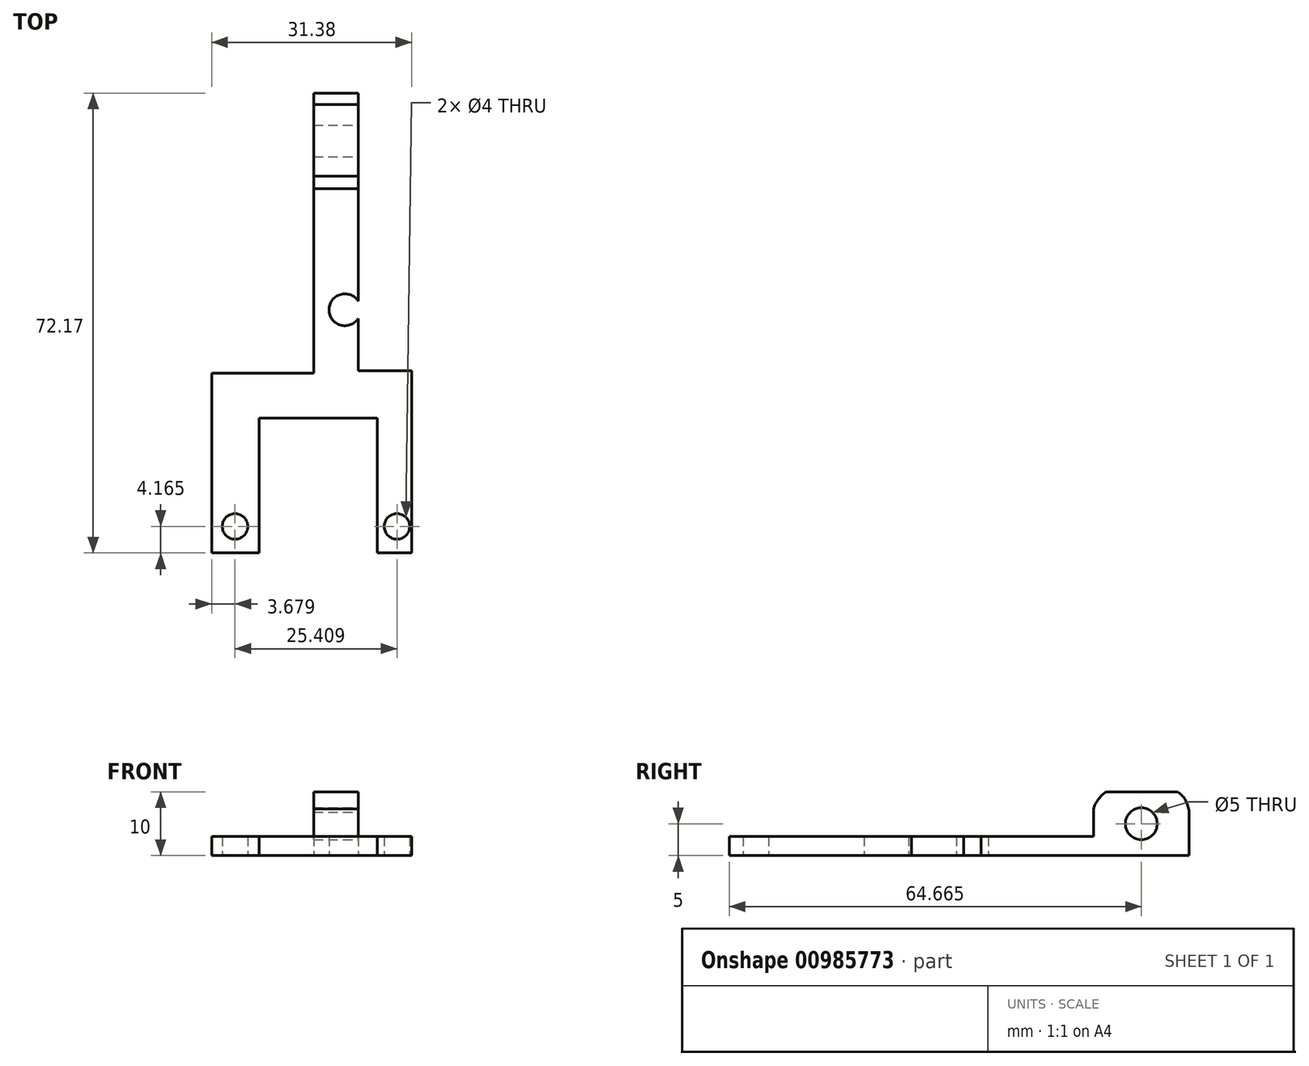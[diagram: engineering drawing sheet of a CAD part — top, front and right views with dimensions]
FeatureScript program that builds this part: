
annotation { "Feature Type Name" : "Feature", "Feature Type Description" : "" }
export const myFeature = defineFeature(function(context is Context, id is Id, definition is map)
    precondition{}
    {
        {
            assignVariable(context, id + "F0", {"name" : "thickness", "anyValue" : 3});
        }
        {
            var Q0;
            Q0=qCreatedBy(makeId("Top.planeOp"),FACE);
            var sketch = newSketch(context, id + "F1", { "sketchPlane" : qUnion([Q0])});
            skLineSegment(sketch, "E0", {"start": v(-1.74, 48.16) * mm, "end": v(-1.74, 4.18) * mm});
            skLineSegment(sketch, "E1", {"start": v(-1.74, 4.18) * mm, "end": v(-17.74, 4.18) * mm});
            skLineSegment(sketch, "E2", {"start": v(-17.74, 4.18) * mm, "end": v(-17.74, -24.01) * mm});
            skLineSegment(sketch, "E3", {"start": v(-17.74, -24.01) * mm, "end": v(-10.3, -24.01) * mm});
            skLineSegment(sketch, "E4", {"start": v(-10.3, -24.01) * mm, "end": v(-10.3, -2.82) * mm});
            skLineSegment(sketch, "E5", {"start": v(-10.3, -2.82) * mm, "end": v(8.29, -2.82) * mm});
            skLineSegment(sketch, "E6", {"start": v(8.29, -2.82) * mm, "end": v(8.29, -24.01) * mm});
            skLineSegment(sketch, "E7", {"start": v(8.29, -24.01) * mm, "end": v(13.64, -24.01) * mm});
            skLineSegment(sketch, "E8", {"start": v(13.64, -24.01) * mm, "end": v(13.64, 4.56) * mm});
            skLineSegment(sketch, "E9", {"start": v(13.64, 4.56) * mm, "end": v(5.26, 4.56) * mm});
            skLineSegment(sketch, "E10", {"start": v(5.26, 48.16) * mm, "end": v(-1.74, 48.16) * mm});
            skCircle(sketch, "E11", {"center": v(-14.06, -19.84) * mm, "radius": 2 * mm});
            skCircle(sketch, "E12", {"center": v(11.35, -19.84) * mm, "radius": 2 * mm});
            skLineSegment(sketch, "E13.trimOffspring", {"start": v(5.26, 15.53) * mm, "end": v(5.26, 48.16) * mm});
            skLineSegment(sketch, "E14", {"start": v(5.26, 4.56) * mm, "end": v(5.26, 12.78) * mm});
            skArc(sketch, "E15", {"start": v(5.26, 15.53) * mm, "mid": v(0.67, 14.16) * mm, "end": v(5.26, 12.78) * mm});
            skSolve(sketch);
        }
        {
            var Q0;
            Q0=makeQuery(id+"F1.imprint","IMPRINT",FACE,{"disambiguationData":[TD([[makeQuery(id+"F1.imprint","IMPRINT",EDGE,{"derivedFrom":sQuery(id+"F1.wireOp",EDGE,"E0")}),1.0]])]});
            extrude(context, id + "F2", {"entities" : qUnion([Q0]), "depth" : (getVariable(context, 'thickness')) * mm, "offsetDistance" : 25 * mm});
        }
        {
            var Q0;
            Q0=makeQuery(id+"F2.opExtrude","CAP_FACE",FACE,{"disambiguationData":[OSD([sQuery(id+"F1.wireOp",EDGE,"E0"),sQuery(id+"F1.wireOp",EDGE,"E1"),sQuery(id+"F1.wireOp",EDGE,"E2"),sQuery(id+"F1.wireOp",EDGE,"E3"),sQuery(id+"F1.wireOp",EDGE,"E4"),sQuery(id+"F1.wireOp",EDGE,"E5"),sQuery(id+"F1.wireOp",EDGE,"E6"),sQuery(id+"F1.wireOp",EDGE,"E7"),sQuery(id+"F1.wireOp",EDGE,"E8"),sQuery(id+"F1.wireOp",EDGE,"E9"),sQuery(id+"F1.wireOp",EDGE,"E10"),sQuery(id+"F1.wireOp",EDGE,"E11"),sQuery(id+"F1.wireOp",EDGE,"E12"),sQuery(id+"F1.wireOp",EDGE,"E13.trimOffspring"),sQuery(id+"F1.wireOp",EDGE,"E14"),sQuery(id+"F1.wireOp",EDGE,"E15")])],"isStart":false});
            var sketch = newSketch(context, id + "F3", { "sketchPlane" : qUnion([Q0])});
            skLineSegment(sketch, "E16.bottom", {"start": v(-1.74, 48.16) * mm, "end": v(5.26, 48.16) * mm});
            skLineSegment(sketch, "E16.top", {"start": v(-1.74, 33.16) * mm, "end": v(5.26, 33.16) * mm});
            skLineSegment(sketch, "E16.left", {"start": v(-1.74, 48.16) * mm, "end": v(-1.74, 33.16) * mm});
            skLineSegment(sketch, "E16.right", {"start": v(5.26, 48.16) * mm, "end": v(5.26, 33.16) * mm});
            skSolve(sketch);
        }
        {
            var Q0;
            Q0=makeQuery(id+"F3.imprint","IMPRINT",FACE,{"disambiguationData":[TD([[makeQuery(id+"F3.imprint","IMPRINT",EDGE,{"derivedFrom":sQuery(id+"F3.wireOp",EDGE,"E16.bottom")}),1.0]])]});
            extrude(context, id + "F4", {"entities" : qUnion([Q0]), "operationType" : NewBodyOperationType.ADD, "depth" : (10 - getVariable(context, 'thickness')) * mm, "offsetDistance" : 25 * mm});
        }
        {
            var Q0;
            Q0=makeQuery(id+"F4.boolean.opBoolean","MERGE",FACE,{"derivedFrom":[makeQuery(id+"F2.opExtrude","SWEPT_FACE",FACE,{"disambiguationData":[OSD([sQuery(id+"F1.wireOp",EDGE,"E13.trimOffspring")])]}),makeQuery(id+"F4.opExtrude","SWEPT_FACE",FACE,{"disambiguationData":[OSD([sQuery(id+"F3.wireOp",EDGE,"E16.right")])]})]});
            var sketch = newSketch(context, id + "F5", { "sketchPlane" : qUnion([Q0])});
            skCircle(sketch, "E17", {"center": v(40.66, 5) * mm, "radius": 2.5 * mm});
            skPoint(sketch, "E18", {"position": v(40.66, 10) * mm});
            skPoint(sketch, "E19", {"position": v(48.16, 5) * mm});
            skSolve(sketch);
        }
        {
            var Q0;
            Q0=makeQuery(id+"F5.imprint","IMPRINT",FACE,{"disambiguationData":[TD([[makeQuery(id+"F5.imprint","IMPRINT",EDGE,{"derivedFrom":sQuery(id+"F5.wireOp",EDGE,"E17")}),1.0]])]});
            var Q1;
            Q1=makeQuery(id+"F4.boolean.opBoolean","MERGE",FACE,{"derivedFrom":[makeQuery(id+"F2.opExtrude","SWEPT_FACE",FACE,{"disambiguationData":[OSD([sQuery(id+"F1.wireOp",EDGE,"E0")])]}),makeQuery(id+"F4.opExtrude","SWEPT_FACE",FACE,{"disambiguationData":[OSD([sQuery(id+"F3.wireOp",EDGE,"E16.left")])]})]});
            extrude(context, id + "F6", {"entities" : qUnion([Q0]), "operationType" : NewBodyOperationType.REMOVE, "endBound" : BoundingType.UP_TO_SURFACE, "oppositeDirection" : true, "depth" : 25 * mm, "endBoundEntityFace" : qUnion([Q1]), "offsetDistance" : 25 * mm});
        }
        {
            var Q0;
            Q0=makeQuery(id+"F4.boolean.opBoolean","MERGE",FACE,{"derivedFrom":[makeQuery(id+"F2.opExtrude","SWEPT_FACE",FACE,{"disambiguationData":[OSD([sQuery(id+"F1.wireOp",EDGE,"E13.trimOffspring")])]}),makeQuery(id+"F4.opExtrude","SWEPT_FACE",FACE,{"disambiguationData":[OSD([sQuery(id+"F3.wireOp",EDGE,"E16.right")])]})]});
            var sketch = newSketch(context, id + "F7", { "sketchPlane" : qUnion([Q0])});
            skArc(sketch, "E20", {"start": v(35.1, 10) * mm, "mid": v(33.92, 8.83) * mm, "end": v(33.16, 7.35) * mm});
            skArc(sketch, "E21", {"start": v(48.16, 6.84) * mm, "mid": v(47.63, 8.62) * mm, "end": v(46.38, 10) * mm});
            skSolve(sketch);
        }
        {
            var Q0;
            {var subQ0=sQuery(id+"F7.wireOp",EDGE,"E20");Q0=makeQuery(id+"F7.imprint","IMPRINT",FACE,{"disambiguationData":[TD([[makeQuery(id+"F7.imprint","IMPRINT",EDGE,{"derivedFrom":subQ0}),-1.0]])]});}
            var Q1;
            {var subQ0=sQuery(id+"F7.wireOp",EDGE,"E21");Q1=makeQuery(id+"F7.imprint","IMPRINT",FACE,{"disambiguationData":[TD([[makeQuery(id+"F7.imprint","IMPRINT",EDGE,{"derivedFrom":subQ0}),-1.0]])]});}
            extrude(context, id + "F8", {"entities" : qUnion([Q0, Q1]), "operationType" : NewBodyOperationType.REMOVE, "oppositeDirection" : true, "depth" : 25 * mm, "offsetDistance" : 25 * mm});
        }
    });
